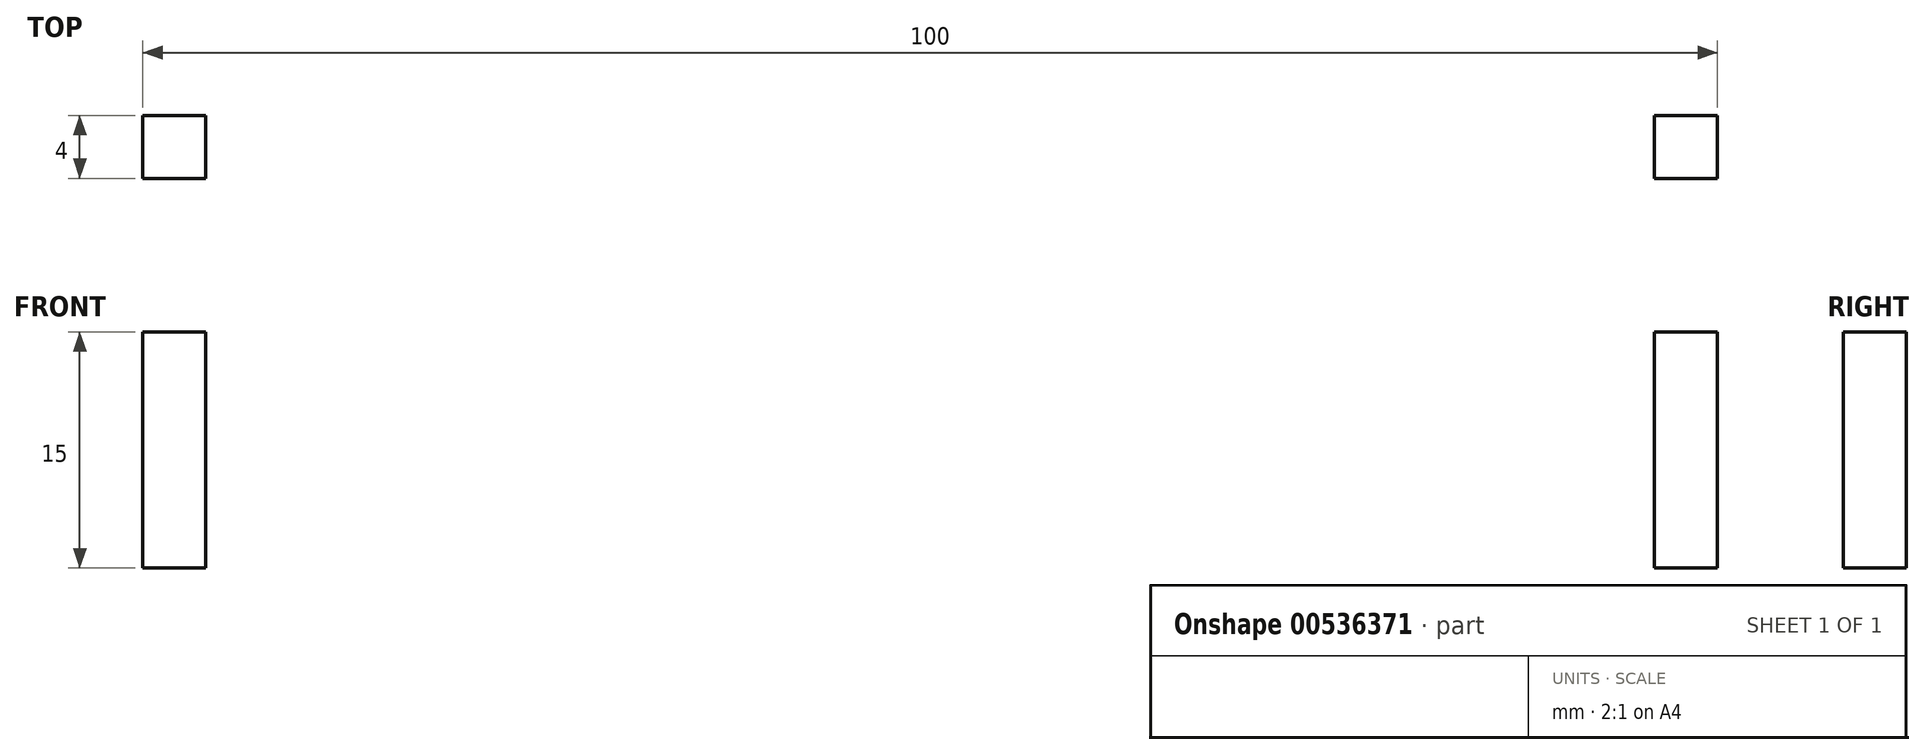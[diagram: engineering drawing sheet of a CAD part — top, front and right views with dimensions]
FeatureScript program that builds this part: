
annotation { "Feature Type Name" : "Feature", "Feature Type Description" : "" }
export const myFeature = defineFeature(function(context is Context, id is Id, definition is map)
    precondition{}
    {
        {
            var Q0;
            Q0=qCreatedBy(makeId("Front.planeOp"),FACE);
            var sketch = newSketch(context, id + "F0", { "sketchPlane" : qUnion([Q0])});
            skLineSegment(sketch, "E0.bottom", {"start": v(0, 0) * mm, "end": v(100, 0) * mm});
            skLineSegment(sketch, "E0.top", {"start": v(0, 50) * mm, "end": v(100, 50) * mm});
            skLineSegment(sketch, "E0.left", {"start": v(0, 0) * mm, "end": v(0, 50) * mm});
            skLineSegment(sketch, "E0.right", {"start": v(100, 0) * mm, "end": v(100, 50) * mm});
            skLineSegment(sketch, "E1.bottom", {"start": v(0, 50) * mm, "end": v(4, 50) * mm});
            skLineSegment(sketch, "E1.top", {"start": v(0, 35) * mm, "end": v(4, 35) * mm});
            skLineSegment(sketch, "E1.left", {"start": v(0, 50) * mm, "end": v(0, 35) * mm});
            skLineSegment(sketch, "E1.right", {"start": v(4, 50) * mm, "end": v(4, 35) * mm});
            skLineSegment(sketch, "E2.bottom", {"start": v(100, 50) * mm, "end": v(96, 50) * mm});
            skLineSegment(sketch, "E2.top", {"start": v(100, 35) * mm, "end": v(96, 35) * mm});
            skLineSegment(sketch, "E2.left", {"start": v(100, 50) * mm, "end": v(100, 35) * mm});
            skLineSegment(sketch, "E2.right", {"start": v(96, 50) * mm, "end": v(96, 35) * mm});
            skLineSegment(sketch, "E3.bottom", {"start": v(0, 0) * mm, "end": v(20, 0) * mm});
            skLineSegment(sketch, "E3.top", {"start": v(0, 4) * mm, "end": v(20, 4) * mm});
            skLineSegment(sketch, "E3.left", {"start": v(0, 0) * mm, "end": v(0, 4) * mm});
            skLineSegment(sketch, "E3.right", {"start": v(20, 0) * mm, "end": v(20, 4) * mm});
            skLineSegment(sketch, "E4.bottom", {"start": v(100, 0) * mm, "end": v(80, 0) * mm});
            skLineSegment(sketch, "E4.top", {"start": v(100, 4) * mm, "end": v(80, 4) * mm});
            skLineSegment(sketch, "E4.left", {"start": v(100, 0) * mm, "end": v(100, 4) * mm});
            skLineSegment(sketch, "E4.right", {"start": v(80, 0) * mm, "end": v(80, 4) * mm});
            skLineSegment(sketch, "E5.bottom", {"start": v(60, 0) * mm, "end": v(40, 0) * mm});
            skLineSegment(sketch, "E5.top", {"start": v(60, 4) * mm, "end": v(40, 4) * mm});
            skLineSegment(sketch, "E5.left", {"start": v(60, 0) * mm, "end": v(60, 4) * mm});
            skLineSegment(sketch, "E5.right", {"start": v(40, 0) * mm, "end": v(40, 4) * mm});
            skLineSegment(sketch, "E6.bottom", {"start": v(0, 4) * mm, "end": v(4, 4) * mm});
            skLineSegment(sketch, "E6.top", {"start": v(0, 19) * mm, "end": v(4, 19) * mm});
            skLineSegment(sketch, "E6.left", {"start": v(0, 4) * mm, "end": v(0, 19) * mm});
            skLineSegment(sketch, "E6.right", {"start": v(4, 4) * mm, "end": v(4, 19) * mm});
            skLineSegment(sketch, "E7.bottom", {"start": v(100, 4) * mm, "end": v(96, 4) * mm});
            skLineSegment(sketch, "E7.top", {"start": v(100, 19) * mm, "end": v(96, 19) * mm});
            skLineSegment(sketch, "E7.left", {"start": v(100, 4) * mm, "end": v(100, 19) * mm});
            skLineSegment(sketch, "E7.right", {"start": v(96, 4) * mm, "end": v(96, 19) * mm});
            skSolve(sketch);
        }
        {
            var Q0;
            Q0=makeQuery(id+"F0.imprint","IMPRINT",FACE,{"disambiguationData":[TD([[makeQuery(id+"F0.imprint","IMPRINT",EDGE,{"derivedFrom":sQuery(id+"F0.wireOp",EDGE,"E0.top")}),-1.0]])]});
            extrude(context, id + "F1", {"entities" : qUnion([Q0]), "depth" : 4 * mm, "offsetDistance" : 25 * mm});
        }
    });
